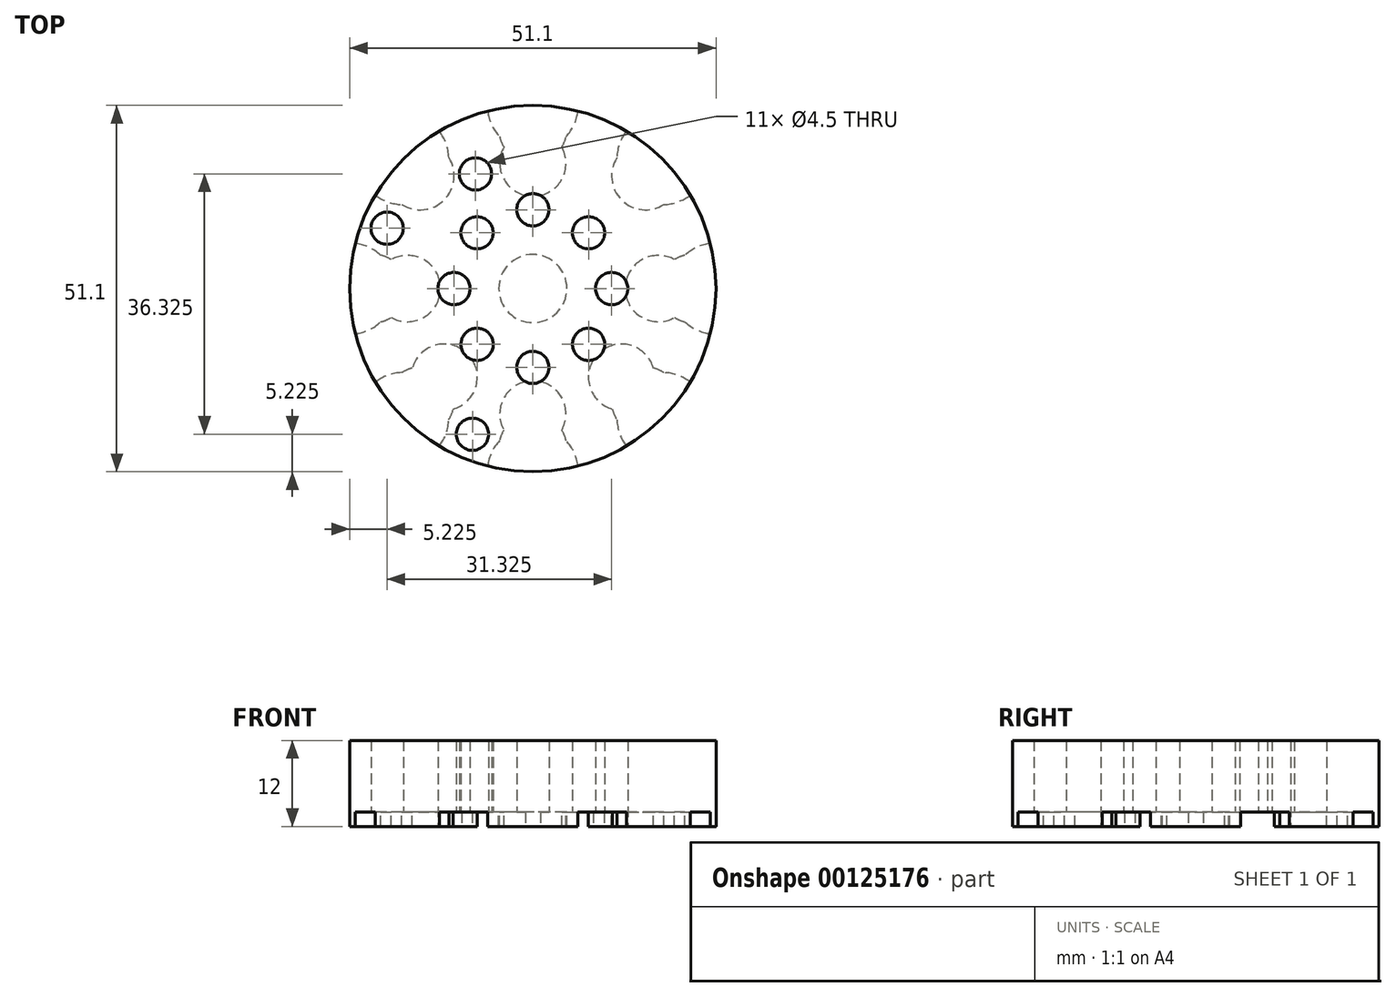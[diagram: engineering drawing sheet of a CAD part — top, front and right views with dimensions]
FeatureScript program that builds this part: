
annotation { "Feature Type Name" : "Feature", "Feature Type Description" : "" }
export const myFeature = defineFeature(function(context is Context, id is Id, definition is map)
    precondition{}
    {
        {
            var Q0;
            Q0=qCreatedBy(makeId("Top.planeOp"),FACE);
            var sketch = newSketch(context, id + "F0", { "sketchPlane" : qUnion([Q0])});
            skCircle(sketch, "E0", {"center": v(0, 0) * mm, "radius": 4.75 * mm});
            skCircle(sketch, "E1", {"center": v(0, 11) * mm, "radius": 2.25 * mm});
            skCircle(sketch, "E2.1.0", {"center": v(-7.78, 7.78) * mm, "radius": 2.25 * mm});
            skCircle(sketch, "E2.2.0", {"center": v(-11, 0) * mm, "radius": 2.25 * mm});
            skCircle(sketch, "E2.3.0", {"center": v(-7.78, -7.78) * mm, "radius": 2.25 * mm});
            skCircle(sketch, "E2.4.0", {"center": v(0, -11) * mm, "radius": 2.25 * mm});
            skCircle(sketch, "E2.5.0", {"center": v(7.78, -7.78) * mm, "radius": 2.25 * mm});
            skCircle(sketch, "E2.6.0", {"center": v(11, 0) * mm, "radius": 2.25 * mm});
            skCircle(sketch, "E2.7.0", {"center": v(7.78, 7.78) * mm, "radius": 2.25 * mm});
            skCircle(sketch, "E3", {"center": v(-8.42, -20.32) * mm, "radius": 2.25 * mm});
            skCircle(sketch, "E4", {"center": v(-20.32, 8.42) * mm, "radius": 2.25 * mm});
            skCircle(sketch, "E5.MirrorC", {"center": v(8.42, -20.32) * mm, "radius": 2.25 * mm});
            skCircle(sketch, "E6.MirrorC", {"center": v(20.32, 8.42) * mm, "radius": 2.25 * mm});
            skCircle(sketch, "E7", {"center": v(-8, 16) * mm, "radius": 2.25 * mm});
            skCircle(sketch, "E8.MirrorC", {"center": v(8, 16) * mm, "radius": 2.25 * mm});
            skSolve(sketch);
        }
        {
            var Q0;
            Q0=qCreatedBy(makeId("Top.planeOp"),FACE);
            var sketch = newSketch(context, id + "F1", { "sketchPlane" : qUnion([Q0])});
            skCircle(sketch, "E9", {"center": v(0, 25.55) * mm, "radius": 6.35 * mm});
            skCircle(sketch, "E10.1.0", {"center": v(-18.07, 18.07) * mm, "radius": 6.35 * mm});
            skCircle(sketch, "E10.2.0", {"center": v(-25.55, 0) * mm, "radius": 6.35 * mm});
            skCircle(sketch, "E10.3.0", {"center": v(-18.07, -18.07) * mm, "radius": 6.35 * mm});
            skCircle(sketch, "E10.4.0", {"center": v(0, -25.55) * mm, "radius": 6.35 * mm});
            skCircle(sketch, "E10.5.0", {"center": v(18.07, -18.07) * mm, "radius": 6.35 * mm});
            skCircle(sketch, "E10.6.0", {"center": v(25.55, 0) * mm, "radius": 6.35 * mm});
            skCircle(sketch, "E10.7.0", {"center": v(18.07, 18.07) * mm, "radius": 6.35 * mm});
            skPoint(sketch, "E10.center", {"position": v(0, 0) * mm});
            skCircle(sketch, "E11", {"center": v(0, 0) * mm, "radius": 25.55 * mm});
            skSolve(sketch);
        }
        {
            var Q0;
            Q0=qCreatedBy(makeId("Top.planeOp"),FACE);
            var sketch = newSketch(context, id + "F2", { "sketchPlane" : qUnion([Q0])});
            skCircle(sketch, "E12", {"center": v(0, 22.25) * mm, "radius": 4.75 * mm});
            skCircle(sketch, "E13.1.0", {"center": v(-15.73, 15.73) * mm, "radius": 4.75 * mm});
            skCircle(sketch, "E13.2.0", {"center": v(-22.25, 0) * mm, "radius": 4.75 * mm});
            skCircle(sketch, "E13.3.0", {"center": v(-15.73, -15.73) * mm, "radius": 4.75 * mm});
            skCircle(sketch, "E13.4.0", {"center": v(0, -22.25) * mm, "radius": 4.75 * mm});
            skCircle(sketch, "E13.5.0", {"center": v(15.73, -15.73) * mm, "radius": 4.75 * mm});
            skCircle(sketch, "E13.6.0", {"center": v(22.25, 0) * mm, "radius": 4.75 * mm});
            skCircle(sketch, "E13.7.0", {"center": v(15.73, 15.73) * mm, "radius": 4.75 * mm});
            skPoint(sketch, "E13.center", {"position": v(0, 0) * mm});
            skCircle(sketch, "E14", {"center": v(0, 0) * mm, "radius": 25 * mm});
            skSolve(sketch);
        }
        {
            var Q0;
            Q0=qCreatedBy(makeId("Top.planeOp"),FACE);
            var sketch = newSketch(context, id + "F3", { "sketchPlane" : qUnion([Q0])});
            skCircle(sketch, "E15", {"center": v(0, 17.5) * mm, "radius": 4.62 * mm});
            skCircle(sketch, "E16.1.0", {"center": v(-12.37, 12.37) * mm, "radius": 4.62 * mm});
            skCircle(sketch, "E16.2.0", {"center": v(-17.5, 0) * mm, "radius": 4.62 * mm});
            skCircle(sketch, "E16.3.0", {"center": v(-12.37, -12.37) * mm, "radius": 4.62 * mm});
            skCircle(sketch, "E16.4.0", {"center": v(0, -17.5) * mm, "radius": 4.62 * mm});
            skCircle(sketch, "E16.5.0", {"center": v(12.37, -12.37) * mm, "radius": 4.62 * mm});
            skCircle(sketch, "E16.6.0", {"center": v(17.5, 0) * mm, "radius": 4.62 * mm});
            skCircle(sketch, "E16.7.0", {"center": v(12.37, 12.37) * mm, "radius": 4.62 * mm});
            skPoint(sketch, "E16.center", {"position": v(0, 0) * mm});
            skCircle(sketch, "E17", {"center": v(0, 0) * mm, "radius": 25 * mm});
            skSolve(sketch);
        }
        {
            var Q0;
            {var subQ0=sQuery(id+"F1.wireOp",EDGE,"E11");var subQ1=sQuery(id+"F1.wireOp",EDGE,"E9");var subQ2=makeQuery(id+"F1.imprint","INTERSECT",VERTEX,{"disambiguationData":[OD(0.0)],"derivedFrom":[subQ1,subQ0]});Q0=makeQuery(id+"F1.imprint","IMPRINT",FACE,{"disambiguationData":[TD([[makeQuery(id+"F1.imprint","IMPRINT",EDGE,{"disambiguationData":[TD([[subQ2,1.0]])],"derivedFrom":subQ1}),1.0]])]});}
            var Q1;
            {var subQ0=sQuery(id+"F1.wireOp",EDGE,"E11");var subQ1=sQuery(id+"F1.wireOp",EDGE,"E10.1.0");var subQ2=makeQuery(id+"F1.imprint","INTERSECT",VERTEX,{"disambiguationData":[OD(0.0)],"derivedFrom":[subQ1,subQ0]});Q1=makeQuery(id+"F1.imprint","IMPRINT",FACE,{"disambiguationData":[TD([[makeQuery(id+"F1.imprint","IMPRINT",EDGE,{"disambiguationData":[TD([[subQ2,1.0]])],"derivedFrom":subQ1}),1.0]])]});}
            var Q2;
            {var subQ0=sQuery(id+"F1.wireOp",EDGE,"E11");var subQ1=sQuery(id+"F1.wireOp",EDGE,"E10.2.0");var subQ2=makeQuery(id+"F1.imprint","INTERSECT",VERTEX,{"disambiguationData":[OD(0.0)],"derivedFrom":[subQ1,subQ0]});Q2=makeQuery(id+"F1.imprint","IMPRINT",FACE,{"disambiguationData":[TD([[makeQuery(id+"F1.imprint","IMPRINT",EDGE,{"disambiguationData":[TD([[subQ2,1.0]])],"derivedFrom":subQ1}),1.0]])]});}
            var Q3;
            {var subQ0=sQuery(id+"F1.wireOp",EDGE,"E11");var subQ1=sQuery(id+"F1.wireOp",EDGE,"E10.3.0");var subQ2=makeQuery(id+"F1.imprint","INTERSECT",VERTEX,{"disambiguationData":[OD(0.0)],"derivedFrom":[subQ1,subQ0]});Q3=makeQuery(id+"F1.imprint","IMPRINT",FACE,{"disambiguationData":[TD([[makeQuery(id+"F1.imprint","IMPRINT",EDGE,{"disambiguationData":[TD([[subQ2,1.0]])],"derivedFrom":subQ1}),1.0]])]});}
            var Q4;
            {var subQ0=sQuery(id+"F1.wireOp",EDGE,"E11");var subQ1=sQuery(id+"F1.wireOp",EDGE,"E10.4.0");var subQ2=makeQuery(id+"F1.imprint","INTERSECT",VERTEX,{"disambiguationData":[OD(0.0)],"derivedFrom":[subQ1,subQ0]});Q4=makeQuery(id+"F1.imprint","IMPRINT",FACE,{"disambiguationData":[TD([[makeQuery(id+"F1.imprint","IMPRINT",EDGE,{"disambiguationData":[TD([[subQ2,1.0]])],"derivedFrom":subQ1}),1.0]])]});}
            var Q5;
            {var subQ0=sQuery(id+"F1.wireOp",EDGE,"E11");var subQ1=sQuery(id+"F1.wireOp",EDGE,"E10.5.0");var subQ2=makeQuery(id+"F1.imprint","INTERSECT",VERTEX,{"disambiguationData":[OD(0.0)],"derivedFrom":[subQ1,subQ0]});Q5=makeQuery(id+"F1.imprint","IMPRINT",FACE,{"disambiguationData":[TD([[makeQuery(id+"F1.imprint","IMPRINT",EDGE,{"disambiguationData":[TD([[subQ2,1.0]])],"derivedFrom":subQ1}),1.0]])]});}
            var Q6;
            {var subQ0=sQuery(id+"F1.wireOp",EDGE,"E11");var subQ1=sQuery(id+"F1.wireOp",EDGE,"E10.6.0");var subQ2=makeQuery(id+"F1.imprint","INTERSECT",VERTEX,{"disambiguationData":[OD(0.0)],"derivedFrom":[subQ1,subQ0]});Q6=makeQuery(id+"F1.imprint","IMPRINT",FACE,{"disambiguationData":[TD([[makeQuery(id+"F1.imprint","IMPRINT",EDGE,{"disambiguationData":[TD([[subQ2,-1.0]])],"derivedFrom":subQ1}),1.0]])]});}
            var Q7;
            {var subQ0=sQuery(id+"F1.wireOp",EDGE,"E11");var subQ1=sQuery(id+"F1.wireOp",EDGE,"E10.7.0");var subQ2=makeQuery(id+"F1.imprint","INTERSECT",VERTEX,{"disambiguationData":[OD(0.0)],"derivedFrom":[subQ1,subQ0]});Q7=makeQuery(id+"F1.imprint","IMPRINT",FACE,{"disambiguationData":[TD([[makeQuery(id+"F1.imprint","IMPRINT",EDGE,{"disambiguationData":[TD([[subQ2,1.0]])],"derivedFrom":subQ1}),1.0]])]});}
            var Q8;
            Q8=makeQuery(id+"F0.imprint","IMPRINT",FACE,{"disambiguationData":[TD([[makeQuery(id+"F0.imprint","IMPRINT",EDGE,{"derivedFrom":sQuery(id+"F0.wireOp",EDGE,"E0")}),1.0]])]});
            extrude(context, id + "F4", {"entities" : qUnion([Q0, Q1, Q2, Q3, Q4, Q5, Q6, Q7, Q8]), "oppositeDirection" : true, "depth" : 2 * mm});
        }
        {
            var Q0;
            {var subQ0=sQuery(id+"F1.wireOp",EDGE,"E11");var subQ1=sQuery(id+"F1.wireOp",EDGE,"E10.6.0");var subQ2=makeQuery(id+"F1.imprint","INTERSECT",VERTEX,{"disambiguationData":[OD(0.0)],"derivedFrom":[subQ1,subQ0]});Q0=makeQuery(id+"F1.imprint","IMPRINT",FACE,{"disambiguationData":[TD([[makeQuery(id+"F1.imprint","IMPRINT",EDGE,{"disambiguationData":[TD([[subQ2,-1.0]])],"derivedFrom":subQ1}),1.0]])]});}
            var Q1;
            {var subQ0=sQuery(id+"F1.wireOp",EDGE,"E11");var subQ1=sQuery(id+"F1.wireOp",EDGE,"E10.7.0");var subQ2=makeQuery(id+"F1.imprint","INTERSECT",VERTEX,{"disambiguationData":[OD(0.0)],"derivedFrom":[subQ1,subQ0]});Q1=makeQuery(id+"F1.imprint","IMPRINT",FACE,{"disambiguationData":[TD([[makeQuery(id+"F1.imprint","IMPRINT",EDGE,{"disambiguationData":[TD([[subQ2,1.0]])],"derivedFrom":subQ1}),1.0]])]});}
            var Q2;
            {var subQ0=sQuery(id+"F1.wireOp",EDGE,"E11");var subQ1=sQuery(id+"F1.wireOp",EDGE,"E9");var subQ2=makeQuery(id+"F1.imprint","INTERSECT",VERTEX,{"disambiguationData":[OD(0.0)],"derivedFrom":[subQ1,subQ0]});Q2=makeQuery(id+"F1.imprint","IMPRINT",FACE,{"disambiguationData":[TD([[makeQuery(id+"F1.imprint","IMPRINT",EDGE,{"disambiguationData":[TD([[subQ2,1.0]])],"derivedFrom":subQ1}),1.0]])]});}
            var Q3;
            {var subQ0=sQuery(id+"F1.wireOp",EDGE,"E11");var subQ1=sQuery(id+"F1.wireOp",EDGE,"E10.1.0");var subQ2=makeQuery(id+"F1.imprint","INTERSECT",VERTEX,{"disambiguationData":[OD(0.0)],"derivedFrom":[subQ1,subQ0]});Q3=makeQuery(id+"F1.imprint","IMPRINT",FACE,{"disambiguationData":[TD([[makeQuery(id+"F1.imprint","IMPRINT",EDGE,{"disambiguationData":[TD([[subQ2,1.0]])],"derivedFrom":subQ1}),1.0]])]});}
            var Q4;
            {var subQ0=sQuery(id+"F1.wireOp",EDGE,"E11");var subQ1=sQuery(id+"F1.wireOp",EDGE,"E10.2.0");var subQ2=makeQuery(id+"F1.imprint","INTERSECT",VERTEX,{"disambiguationData":[OD(0.0)],"derivedFrom":[subQ1,subQ0]});Q4=makeQuery(id+"F1.imprint","IMPRINT",FACE,{"disambiguationData":[TD([[makeQuery(id+"F1.imprint","IMPRINT",EDGE,{"disambiguationData":[TD([[subQ2,1.0]])],"derivedFrom":subQ1}),1.0]])]});}
            var Q5;
            {var subQ0=sQuery(id+"F1.wireOp",EDGE,"E11");var subQ1=sQuery(id+"F1.wireOp",EDGE,"E10.3.0");var subQ2=makeQuery(id+"F1.imprint","INTERSECT",VERTEX,{"disambiguationData":[OD(0.0)],"derivedFrom":[subQ1,subQ0]});Q5=makeQuery(id+"F1.imprint","IMPRINT",FACE,{"disambiguationData":[TD([[makeQuery(id+"F1.imprint","IMPRINT",EDGE,{"disambiguationData":[TD([[subQ2,1.0]])],"derivedFrom":subQ1}),1.0]])]});}
            var Q6;
            {var subQ0=sQuery(id+"F1.wireOp",EDGE,"E11");var subQ1=sQuery(id+"F1.wireOp",EDGE,"E10.4.0");var subQ2=makeQuery(id+"F1.imprint","INTERSECT",VERTEX,{"disambiguationData":[OD(0.0)],"derivedFrom":[subQ1,subQ0]});Q6=makeQuery(id+"F1.imprint","IMPRINT",FACE,{"disambiguationData":[TD([[makeQuery(id+"F1.imprint","IMPRINT",EDGE,{"disambiguationData":[TD([[subQ2,1.0]])],"derivedFrom":subQ1}),1.0]])]});}
            var Q7;
            {var subQ0=sQuery(id+"F1.wireOp",EDGE,"E11");var subQ1=sQuery(id+"F1.wireOp",EDGE,"E10.5.0");var subQ2=makeQuery(id+"F1.imprint","INTERSECT",VERTEX,{"disambiguationData":[OD(0.0)],"derivedFrom":[subQ1,subQ0]});Q7=makeQuery(id+"F1.imprint","IMPRINT",FACE,{"disambiguationData":[TD([[makeQuery(id+"F1.imprint","IMPRINT",EDGE,{"disambiguationData":[TD([[subQ2,1.0]])],"derivedFrom":subQ1}),1.0]])]});}
            var Q8;
            {var subQ0=sQuery(id+"F1.wireOp",EDGE,"E11");var subQ7=sQuery(id+"F1.wireOp",EDGE,"E9");var subQ8=makeQuery(id+"F1.imprint","INTERSECT",VERTEX,{"disambiguationData":[OD(0.0)],"derivedFrom":[subQ7,subQ0]});Q8=makeQuery(id+"F1.imprint","IMPRINT",FACE,{"disambiguationData":[TD([[makeQuery(id+"F1.imprint","IMPRINT",EDGE,{"disambiguationData":[TD([[subQ8,1.0]])],"derivedFrom":subQ7}),-1.0]])]});}
            extrude(context, id + "F5", {"entities" : qUnion([Q0, Q1, Q2, Q3, Q4, Q5, Q6, Q7, Q8]), "operationType" : NewBodyOperationType.ADD, "depth" : 10 * mm});
        }
        {
            var Q0;
            Q0=makeQuery(id+"F0.imprint","IMPRINT",FACE,{"disambiguationData":[TD([[makeQuery(id+"F0.imprint","IMPRINT",EDGE,{"derivedFrom":sQuery(id+"F0.wireOp",EDGE,"E0")}),1.0]])]});
            var Q1;
            {var subQ0=sQuery(id+"F2.wireOp",EDGE,"SJB64w2r-rFmd-XdKK-IOiA-G3RHLPCS7zPL");var subQ1=sQuery(id+"F2.wireOp",EDGE,"E13.6.0");var subQ2=makeQuery(id+"F2.imprint","INTERSECT",VERTEX,{"disambiguationData":[OD(0.0)],"derivedFrom":[subQ1,subQ0]});Q1=makeQuery(id+"F2.imprint","IMPRINT",FACE,{"disambiguationData":[TD([[makeQuery(id+"F2.imprint","IMPRINT",EDGE,{"disambiguationData":[TD([[subQ2,-1.0]])],"derivedFrom":subQ1}),1.0]])]});}
            var Q2;
            {var subQ0=sQuery(id+"F2.wireOp",EDGE,"SJB64w2r-rFmd-XdKK-IOiA-G3RHLPCS7zPL");var subQ1=sQuery(id+"F2.wireOp",EDGE,"E13.7.0");var subQ2=makeQuery(id+"F2.imprint","INTERSECT",VERTEX,{"disambiguationData":[OD(0.0)],"derivedFrom":[subQ1,subQ0]});Q2=makeQuery(id+"F2.imprint","IMPRINT",FACE,{"disambiguationData":[TD([[makeQuery(id+"F2.imprint","IMPRINT",EDGE,{"disambiguationData":[TD([[subQ2,1.0]])],"derivedFrom":subQ1}),1.0]])]});}
            var Q3;
            {var subQ0=sQuery(id+"F2.wireOp",EDGE,"SJB64w2r-rFmd-XdKK-IOiA-G3RHLPCS7zPL");var subQ1=sQuery(id+"F2.wireOp",EDGE,"E12");var subQ2=makeQuery(id+"F2.imprint","INTERSECT",VERTEX,{"disambiguationData":[OD(0.0)],"derivedFrom":[subQ1,subQ0]});Q3=makeQuery(id+"F2.imprint","IMPRINT",FACE,{"disambiguationData":[TD([[makeQuery(id+"F2.imprint","IMPRINT",EDGE,{"disambiguationData":[TD([[subQ2,1.0]])],"derivedFrom":subQ1}),1.0]])]});}
            var Q4;
            {var subQ0=sQuery(id+"F2.wireOp",EDGE,"SJB64w2r-rFmd-XdKK-IOiA-G3RHLPCS7zPL");var subQ1=sQuery(id+"F2.wireOp",EDGE,"E13.1.0");var subQ2=makeQuery(id+"F2.imprint","INTERSECT",VERTEX,{"disambiguationData":[OD(0.0)],"derivedFrom":[subQ1,subQ0]});Q4=makeQuery(id+"F2.imprint","IMPRINT",FACE,{"disambiguationData":[TD([[makeQuery(id+"F2.imprint","IMPRINT",EDGE,{"disambiguationData":[TD([[subQ2,1.0]])],"derivedFrom":subQ1}),1.0]])]});}
            var Q5;
            {var subQ0=sQuery(id+"F2.wireOp",EDGE,"SJB64w2r-rFmd-XdKK-IOiA-G3RHLPCS7zPL");var subQ1=sQuery(id+"F2.wireOp",EDGE,"E13.2.0");var subQ2=makeQuery(id+"F2.imprint","INTERSECT",VERTEX,{"disambiguationData":[OD(0.0)],"derivedFrom":[subQ1,subQ0]});Q5=makeQuery(id+"F2.imprint","IMPRINT",FACE,{"disambiguationData":[TD([[makeQuery(id+"F2.imprint","IMPRINT",EDGE,{"disambiguationData":[TD([[subQ2,1.0]])],"derivedFrom":subQ1}),1.0]])]});}
            var Q6;
            {var subQ0=sQuery(id+"F2.wireOp",EDGE,"SJB64w2r-rFmd-XdKK-IOiA-G3RHLPCS7zPL");var subQ1=sQuery(id+"F2.wireOp",EDGE,"E13.3.0");var subQ2=makeQuery(id+"F2.imprint","INTERSECT",VERTEX,{"disambiguationData":[OD(0.0)],"derivedFrom":[subQ1,subQ0]});Q6=makeQuery(id+"F2.imprint","IMPRINT",FACE,{"disambiguationData":[TD([[makeQuery(id+"F2.imprint","IMPRINT",EDGE,{"disambiguationData":[TD([[subQ2,1.0]])],"derivedFrom":subQ1}),1.0]])]});}
            var Q7;
            {var subQ0=sQuery(id+"F2.wireOp",EDGE,"SJB64w2r-rFmd-XdKK-IOiA-G3RHLPCS7zPL");var subQ1=sQuery(id+"F2.wireOp",EDGE,"E13.4.0");var subQ2=makeQuery(id+"F2.imprint","INTERSECT",VERTEX,{"disambiguationData":[OD(0.0)],"derivedFrom":[subQ1,subQ0]});Q7=makeQuery(id+"F2.imprint","IMPRINT",FACE,{"disambiguationData":[TD([[makeQuery(id+"F2.imprint","IMPRINT",EDGE,{"disambiguationData":[TD([[subQ2,1.0]])],"derivedFrom":subQ1}),1.0]])]});}
            var Q8;
            {var subQ0=sQuery(id+"F2.wireOp",EDGE,"SJB64w2r-rFmd-XdKK-IOiA-G3RHLPCS7zPL");var subQ1=sQuery(id+"F2.wireOp",EDGE,"E13.5.0");var subQ2=makeQuery(id+"F2.imprint","INTERSECT",VERTEX,{"disambiguationData":[OD(0.0)],"derivedFrom":[subQ1,subQ0]});Q8=makeQuery(id+"F2.imprint","IMPRINT",FACE,{"disambiguationData":[TD([[makeQuery(id+"F2.imprint","IMPRINT",EDGE,{"disambiguationData":[TD([[subQ2,1.0]])],"derivedFrom":subQ1}),1.0]])]});}
            extrude(context, id + "F6", {"entities" : qUnion([Q0, Q1, Q2, Q3, Q4, Q5, Q6, Q7, Q8]), "oppositeDirection" : true, "depth" : 2 * mm});
        }
        {
            var Q0;
            Q0=makeQuery(id+"F3.imprint","IMPRINT",FACE,{"disambiguationData":[TD([[makeQuery(id+"F3.imprint","IMPRINT",EDGE,{"derivedFrom":sQuery(id+"F3.wireOp",EDGE,"E16.5.0")}),1.0]])]});
            var Q1;
            Q1=makeQuery(id+"F3.imprint","IMPRINT",FACE,{"disambiguationData":[TD([[makeQuery(id+"F3.imprint","IMPRINT",EDGE,{"derivedFrom":sQuery(id+"F3.wireOp",EDGE,"E16.4.0")}),1.0]])]});
            var Q2;
            Q2=makeQuery(id+"F3.imprint","IMPRINT",FACE,{"disambiguationData":[TD([[makeQuery(id+"F3.imprint","IMPRINT",EDGE,{"derivedFrom":sQuery(id+"F3.wireOp",EDGE,"E16.3.0")}),1.0]])]});
            var Q3;
            Q3=makeQuery(id+"F3.imprint","IMPRINT",FACE,{"disambiguationData":[TD([[makeQuery(id+"F3.imprint","IMPRINT",EDGE,{"derivedFrom":sQuery(id+"F3.wireOp",EDGE,"E16.2.0")}),1.0]])]});
            var Q4;
            Q4=makeQuery(id+"F3.imprint","IMPRINT",FACE,{"disambiguationData":[TD([[makeQuery(id+"F3.imprint","IMPRINT",EDGE,{"derivedFrom":sQuery(id+"F3.wireOp",EDGE,"E15")}),1.0]])]});
            var Q5;
            Q5=makeQuery(id+"F3.imprint","IMPRINT",FACE,{"disambiguationData":[TD([[makeQuery(id+"F3.imprint","IMPRINT",EDGE,{"derivedFrom":sQuery(id+"F3.wireOp",EDGE,"E16.6.0")}),1.0]])]});
            var Q6;
            Q6=makeQuery(id+"F0.imprint","IMPRINT",FACE,{"disambiguationData":[TD([[makeQuery(id+"F0.imprint","IMPRINT",EDGE,{"derivedFrom":sQuery(id+"F0.wireOp",EDGE,"E0")}),1.0]])]});
            extrude(context, id + "F7", {"entities" : qUnion([Q0, Q1, Q2, Q3, Q4, Q5, Q6]), "oppositeDirection" : true, "depth" : 2 * mm});
        }
        {
            var Q0;
            Q0=makeQuery(id+"F3.imprint","IMPRINT",FACE,{"disambiguationData":[TD([[makeQuery(id+"F3.imprint","IMPRINT",EDGE,{"derivedFrom":sQuery(id+"F3.wireOp",EDGE,"E15")}),-1.0]])]});
            var Q1;
            Q1=makeQuery(id+"F3.imprint","IMPRINT",FACE,{"disambiguationData":[TD([[makeQuery(id+"F3.imprint","IMPRINT",EDGE,{"derivedFrom":sQuery(id+"F3.wireOp",EDGE,"E16.7.0")}),1.0]])]});
            var Q2;
            Q2=makeQuery(id+"F3.imprint","IMPRINT",FACE,{"disambiguationData":[TD([[makeQuery(id+"F3.imprint","IMPRINT",EDGE,{"derivedFrom":sQuery(id+"F3.wireOp",EDGE,"E15")}),1.0]])]});
            var Q3;
            Q3=makeQuery(id+"F3.imprint","IMPRINT",FACE,{"disambiguationData":[TD([[makeQuery(id+"F3.imprint","IMPRINT",EDGE,{"derivedFrom":sQuery(id+"F3.wireOp",EDGE,"E16.1.0")}),1.0]])]});
            var Q4;
            Q4=makeQuery(id+"F3.imprint","IMPRINT",FACE,{"disambiguationData":[TD([[makeQuery(id+"F3.imprint","IMPRINT",EDGE,{"derivedFrom":sQuery(id+"F3.wireOp",EDGE,"E16.2.0")}),1.0]])]});
            var Q5;
            Q5=makeQuery(id+"F3.imprint","IMPRINT",FACE,{"disambiguationData":[TD([[makeQuery(id+"F3.imprint","IMPRINT",EDGE,{"derivedFrom":sQuery(id+"F3.wireOp",EDGE,"E16.3.0")}),1.0]])]});
            var Q6;
            Q6=makeQuery(id+"F3.imprint","IMPRINT",FACE,{"disambiguationData":[TD([[makeQuery(id+"F3.imprint","IMPRINT",EDGE,{"derivedFrom":sQuery(id+"F3.wireOp",EDGE,"E16.4.0")}),1.0]])]});
            var Q7;
            Q7=makeQuery(id+"F3.imprint","IMPRINT",FACE,{"disambiguationData":[TD([[makeQuery(id+"F3.imprint","IMPRINT",EDGE,{"derivedFrom":sQuery(id+"F3.wireOp",EDGE,"E16.5.0")}),1.0]])]});
            var Q8;
            Q8=makeQuery(id+"F3.imprint","IMPRINT",FACE,{"disambiguationData":[TD([[makeQuery(id+"F3.imprint","IMPRINT",EDGE,{"derivedFrom":sQuery(id+"F3.wireOp",EDGE,"E16.6.0")}),1.0]])]});
            var Q9;
            Q9=makeQuery(id+"F0.imprint","IMPRINT",FACE,{"disambiguationData":[TD([[makeQuery(id+"F0.imprint","IMPRINT",EDGE,{"derivedFrom":sQuery(id+"F0.wireOp",EDGE,"E0")}),1.0]])]});
            extrude(context, id + "F8", {"entities" : qUnion([Q0, Q1, Q2, Q3, Q4, Q5, Q6, Q7, Q8, Q9]), "operationType" : NewBodyOperationType.ADD, "depth" : 10 * mm});
        }
        {
            var Q0;
            {var subQ0=sQuery(id+"F2.wireOp",EDGE,"SJB64w2r-rFmd-XdKK-IOiA-G3RHLPCS7zPL");var subQ1=sQuery(id+"F2.wireOp",EDGE,"E12");var subQ2=makeQuery(id+"F2.imprint","INTERSECT",VERTEX,{"disambiguationData":[OD(0.0)],"derivedFrom":[subQ1,subQ0]});Q0=makeQuery(id+"F2.imprint","IMPRINT",FACE,{"disambiguationData":[TD([[makeQuery(id+"F2.imprint","IMPRINT",EDGE,{"disambiguationData":[TD([[subQ2,1.0]])],"derivedFrom":subQ1}),-1.0]])]});}
            var Q1;
            {var subQ0=sQuery(id+"F2.wireOp",EDGE,"SJB64w2r-rFmd-XdKK-IOiA-G3RHLPCS7zPL");var subQ1=sQuery(id+"F2.wireOp",EDGE,"E13.3.0");var subQ2=makeQuery(id+"F2.imprint","INTERSECT",VERTEX,{"disambiguationData":[OD(0.0)],"derivedFrom":[subQ1,subQ0]});Q1=makeQuery(id+"F2.imprint","IMPRINT",FACE,{"disambiguationData":[TD([[makeQuery(id+"F2.imprint","IMPRINT",EDGE,{"disambiguationData":[TD([[subQ2,1.0]])],"derivedFrom":subQ1}),1.0]])]});}
            var Q2;
            {var subQ0=sQuery(id+"F2.wireOp",EDGE,"SJB64w2r-rFmd-XdKK-IOiA-G3RHLPCS7zPL");var subQ1=sQuery(id+"F2.wireOp",EDGE,"E13.4.0");var subQ2=makeQuery(id+"F2.imprint","INTERSECT",VERTEX,{"disambiguationData":[OD(0.0)],"derivedFrom":[subQ1,subQ0]});Q2=makeQuery(id+"F2.imprint","IMPRINT",FACE,{"disambiguationData":[TD([[makeQuery(id+"F2.imprint","IMPRINT",EDGE,{"disambiguationData":[TD([[subQ2,1.0]])],"derivedFrom":subQ1}),1.0]])]});}
            var Q3;
            {var subQ0=sQuery(id+"F2.wireOp",EDGE,"SJB64w2r-rFmd-XdKK-IOiA-G3RHLPCS7zPL");var subQ1=sQuery(id+"F2.wireOp",EDGE,"E13.5.0");var subQ2=makeQuery(id+"F2.imprint","INTERSECT",VERTEX,{"disambiguationData":[OD(0.0)],"derivedFrom":[subQ1,subQ0]});Q3=makeQuery(id+"F2.imprint","IMPRINT",FACE,{"disambiguationData":[TD([[makeQuery(id+"F2.imprint","IMPRINT",EDGE,{"disambiguationData":[TD([[subQ2,1.0]])],"derivedFrom":subQ1}),1.0]])]});}
            var Q4;
            {var subQ0=sQuery(id+"F2.wireOp",EDGE,"SJB64w2r-rFmd-XdKK-IOiA-G3RHLPCS7zPL");var subQ1=sQuery(id+"F2.wireOp",EDGE,"E13.6.0");var subQ2=makeQuery(id+"F2.imprint","INTERSECT",VERTEX,{"disambiguationData":[OD(0.0)],"derivedFrom":[subQ1,subQ0]});Q4=makeQuery(id+"F2.imprint","IMPRINT",FACE,{"disambiguationData":[TD([[makeQuery(id+"F2.imprint","IMPRINT",EDGE,{"disambiguationData":[TD([[subQ2,-1.0]])],"derivedFrom":subQ1}),1.0]])]});}
            var Q5;
            {var subQ0=sQuery(id+"F2.wireOp",EDGE,"SJB64w2r-rFmd-XdKK-IOiA-G3RHLPCS7zPL");var subQ1=sQuery(id+"F2.wireOp",EDGE,"E13.7.0");var subQ2=makeQuery(id+"F2.imprint","INTERSECT",VERTEX,{"disambiguationData":[OD(0.0)],"derivedFrom":[subQ1,subQ0]});Q5=makeQuery(id+"F2.imprint","IMPRINT",FACE,{"disambiguationData":[TD([[makeQuery(id+"F2.imprint","IMPRINT",EDGE,{"disambiguationData":[TD([[subQ2,1.0]])],"derivedFrom":subQ1}),1.0]])]});}
            var Q6;
            {var subQ0=sQuery(id+"F2.wireOp",EDGE,"SJB64w2r-rFmd-XdKK-IOiA-G3RHLPCS7zPL");var subQ1=sQuery(id+"F2.wireOp",EDGE,"E12");var subQ2=makeQuery(id+"F2.imprint","INTERSECT",VERTEX,{"disambiguationData":[OD(0.0)],"derivedFrom":[subQ1,subQ0]});Q6=makeQuery(id+"F2.imprint","IMPRINT",FACE,{"disambiguationData":[TD([[makeQuery(id+"F2.imprint","IMPRINT",EDGE,{"disambiguationData":[TD([[subQ2,1.0]])],"derivedFrom":subQ1}),1.0]])]});}
            var Q7;
            {var subQ0=sQuery(id+"F2.wireOp",EDGE,"SJB64w2r-rFmd-XdKK-IOiA-G3RHLPCS7zPL");var subQ1=sQuery(id+"F2.wireOp",EDGE,"E13.1.0");var subQ2=makeQuery(id+"F2.imprint","INTERSECT",VERTEX,{"disambiguationData":[OD(0.0)],"derivedFrom":[subQ1,subQ0]});Q7=makeQuery(id+"F2.imprint","IMPRINT",FACE,{"disambiguationData":[TD([[makeQuery(id+"F2.imprint","IMPRINT",EDGE,{"disambiguationData":[TD([[subQ2,1.0]])],"derivedFrom":subQ1}),1.0]])]});}
            var Q8;
            {var subQ0=sQuery(id+"F2.wireOp",EDGE,"SJB64w2r-rFmd-XdKK-IOiA-G3RHLPCS7zPL");var subQ1=sQuery(id+"F2.wireOp",EDGE,"E13.2.0");var subQ2=makeQuery(id+"F2.imprint","INTERSECT",VERTEX,{"disambiguationData":[OD(0.0)],"derivedFrom":[subQ1,subQ0]});Q8=makeQuery(id+"F2.imprint","IMPRINT",FACE,{"disambiguationData":[TD([[makeQuery(id+"F2.imprint","IMPRINT",EDGE,{"disambiguationData":[TD([[subQ2,1.0]])],"derivedFrom":subQ1}),1.0]])]});}
            var Q9;
            Q9=makeQuery(id+"F0.imprint","IMPRINT",FACE,{"disambiguationData":[TD([[makeQuery(id+"F0.imprint","IMPRINT",EDGE,{"derivedFrom":sQuery(id+"F0.wireOp",EDGE,"E0")}),1.0]])]});
            extrude(context, id + "F9", {"entities" : qUnion([Q0, Q1, Q2, Q3, Q4, Q5, Q6, Q7, Q8, Q9]), "operationType" : NewBodyOperationType.ADD, "depth" : 10 * mm});
        }
        {
            var Q0;
            Q0=makeQuery(id+"F0.imprint","IMPRINT",FACE,{"disambiguationData":[TD([[makeQuery(id+"F0.imprint","IMPRINT",EDGE,{"derivedFrom":sQuery(id+"F0.wireOp",EDGE,"E1")}),1.0]])]});
            var Q1;
            Q1=makeQuery(id+"F0.imprint","IMPRINT",FACE,{"disambiguationData":[TD([[makeQuery(id+"F0.imprint","IMPRINT",EDGE,{"derivedFrom":sQuery(id+"F0.wireOp",EDGE,"E2.1.0")}),1.0]])]});
            var Q2;
            Q2=makeQuery(id+"F0.imprint","IMPRINT",FACE,{"disambiguationData":[TD([[makeQuery(id+"F0.imprint","IMPRINT",EDGE,{"derivedFrom":sQuery(id+"F0.wireOp",EDGE,"E2.2.0")}),1.0]])]});
            var Q3;
            Q3=makeQuery(id+"F0.imprint","IMPRINT",FACE,{"disambiguationData":[TD([[makeQuery(id+"F0.imprint","IMPRINT",EDGE,{"derivedFrom":sQuery(id+"F0.wireOp",EDGE,"E2.3.0")}),1.0]])]});
            var Q4;
            Q4=makeQuery(id+"F0.imprint","IMPRINT",FACE,{"disambiguationData":[TD([[makeQuery(id+"F0.imprint","IMPRINT",EDGE,{"derivedFrom":sQuery(id+"F0.wireOp",EDGE,"E2.4.0")}),1.0]])]});
            var Q5;
            Q5=makeQuery(id+"F0.imprint","IMPRINT",FACE,{"disambiguationData":[TD([[makeQuery(id+"F0.imprint","IMPRINT",EDGE,{"derivedFrom":sQuery(id+"F0.wireOp",EDGE,"E2.5.0")}),1.0]])]});
            var Q6;
            Q6=makeQuery(id+"F0.imprint","IMPRINT",FACE,{"disambiguationData":[TD([[makeQuery(id+"F0.imprint","IMPRINT",EDGE,{"derivedFrom":sQuery(id+"F0.wireOp",EDGE,"E2.6.0")}),1.0]])]});
            var Q7;
            Q7=makeQuery(id+"F0.imprint","IMPRINT",FACE,{"disambiguationData":[TD([[makeQuery(id+"F0.imprint","IMPRINT",EDGE,{"derivedFrom":sQuery(id+"F0.wireOp",EDGE,"E2.7.0")}),1.0]])]});
            var Q8;
            Q8=makeQuery(id+"F0.imprint","IMPRINT",FACE,{"disambiguationData":[TD([[makeQuery(id+"F0.imprint","IMPRINT",EDGE,{"derivedFrom":sQuery(id+"F0.wireOp",EDGE,"E3")}),1.0]])]});
            var Q9;
            Q9=makeQuery(id+"F0.imprint","IMPRINT",FACE,{"disambiguationData":[TD([[makeQuery(id+"F0.imprint","IMPRINT",EDGE,{"derivedFrom":sQuery(id+"F0.wireOp",EDGE,"E5.MirrorC")}),-1.0]])]});
            var Q10;
            Q10=makeQuery(id+"F0.imprint","IMPRINT",FACE,{"disambiguationData":[TD([[makeQuery(id+"F0.imprint","IMPRINT",EDGE,{"derivedFrom":sQuery(id+"F0.wireOp",EDGE,"E6.MirrorC")}),-1.0]])]});
            var Q11;
            Q11=makeQuery(id+"F0.imprint","IMPRINT",FACE,{"disambiguationData":[TD([[makeQuery(id+"F0.imprint","IMPRINT",EDGE,{"derivedFrom":sQuery(id+"F0.wireOp",EDGE,"E7")}),1.0]])]});
            var Q12;
            Q12=makeQuery(id+"F0.imprint","IMPRINT",FACE,{"disambiguationData":[TD([[makeQuery(id+"F0.imprint","IMPRINT",EDGE,{"derivedFrom":sQuery(id+"F0.wireOp",EDGE,"E4")}),1.0]])]});
            var Q13;
            Q13=makeQuery(id+"F0.imprint","IMPRINT",FACE,{"disambiguationData":[TD([[makeQuery(id+"F0.imprint","IMPRINT",EDGE,{"derivedFrom":sQuery(id+"F0.wireOp",EDGE,"E8.MirrorC")}),-1.0]])]});
            extrude(context, id + "F10", {"entities" : qUnion([Q0, Q1, Q2, Q3, Q4, Q5, Q6, Q7, Q8, Q9, Q10, Q11, Q12, Q13]), "operationType" : NewBodyOperationType.REMOVE, "endBound" : BoundingType.SYMMETRIC, "depth" : 25 * mm});
        }
    });
